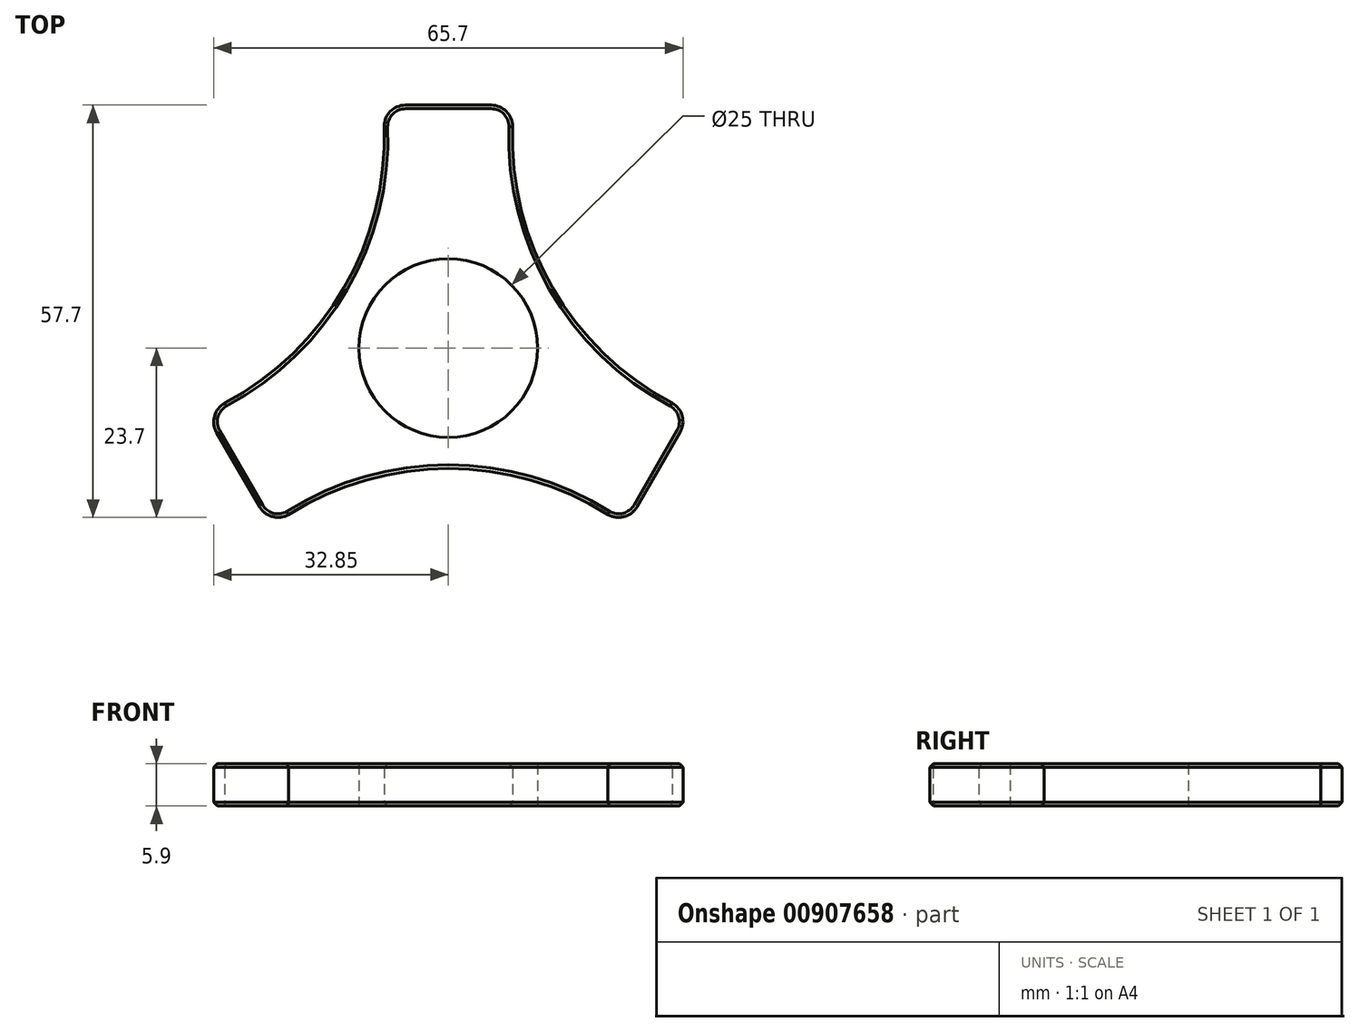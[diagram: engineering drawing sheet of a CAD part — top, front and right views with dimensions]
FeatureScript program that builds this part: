
annotation { "Feature Type Name" : "Feature", "Feature Type Description" : "" }
export const myFeature = defineFeature(function(context is Context, id is Id, definition is map)
    precondition{}
    {
        {
            var Q0;
            Q0=qCreatedBy(makeId("Top.planeOp"),FACE);
            var sketch = newSketch(context, id + "F0", { "sketchPlane" : qUnion([Q0])});
            skPoint(sketch, "E0.center", {"position": v(0, 0) * mm});
            skLineSegment(sketch, "E1", {"start": v(0, 35) * mm, "end": v(0, 0) * mm, "construction": true});
            skArc(sketch, "E2.0", {"start": v(-6, 34) * mm, "mid": v(-8.12, 33.12) * mm, "end": v(-9, 31) * mm});
            skLineSegment(sketch, "E3.0", {"start": v(-6, 34) * mm, "end": v(6, 34) * mm});
            skArc(sketch, "E4.MirrorCS", {"start": v(6, 34) * mm, "mid": v(8.12, 33.12) * mm, "end": v(9, 31) * mm});
            skArc(sketch, "E5.1.0", {"start": v(-26.44, -22.2) * mm, "mid": v(-24.62, -23.6) * mm, "end": v(-22.35, -23.3) * mm});
            skLineSegment(sketch, "E5.1.1", {"start": v(-26.44, -22.2) * mm, "end": v(-32.44, -11.8) * mm});
            skArc(sketch, "E5.1.2", {"start": v(-32.44, -11.8) * mm, "mid": v(-32.74, -9.53) * mm, "end": v(-31.35, -7.7) * mm});
            skArc(sketch, "E5.2.0", {"start": v(32.44, -11.8) * mm, "mid": v(32.74, -9.53) * mm, "end": v(31.35, -7.7) * mm});
            skLineSegment(sketch, "E5.2.1", {"start": v(32.44, -11.8) * mm, "end": v(26.44, -22.2) * mm});
            skArc(sketch, "E5.2.2", {"start": v(26.44, -22.2) * mm, "mid": v(24.62, -23.6) * mm, "end": v(22.35, -23.3) * mm});
            skArc(sketch, "E6", {"start": v(-31.35, -7.7) * mm, "mid": v(-14.6, 8.43) * mm, "end": v(-9, 31) * mm});
            skArc(sketch, "E7.MirrorCS", {"start": v(31.35, -7.7) * mm, "mid": v(14.6, 8.43) * mm, "end": v(9, 31) * mm});
            skArc(sketch, "E8", {"start": v(22.35, -23.3) * mm, "mid": v(0, -16.86) * mm, "end": v(-22.35, -23.3) * mm});
            skCircle(sketch, "E9", {"center": v(0, 0) * mm, "radius": 12.5 * mm});
            skSolve(sketch);
        }
        {
            var Q0;
            Q0 = qSketchRegion(id + "F0", true);
            extrude(context, id + "F1", {"entities" : qUnion([Q0]), "depth" : 5.9 * mm, "offsetDistance" : 25 * mm});
        }
        {
            var Q0;
            Q0=makeQuery(id+"F1.opExtrude","CAP_EDGE",EDGE,{"disambiguationData":[OSD([sQuery(id+"F0.wireOp",EDGE,"E6")])],"isStart":false});
            var Q1;
            Q1=makeQuery(id+"F1.opExtrude","CAP_EDGE",EDGE,{"disambiguationData":[OSD([sQuery(id+"F0.wireOp",EDGE,"E2.0")])],"isStart":false});
            var Q2;
            Q2=makeQuery(id+"F1.opExtrude","CAP_EDGE",EDGE,{"disambiguationData":[OSD([sQuery(id+"F0.wireOp",EDGE,"E3.0")])],"isStart":false});
            var Q3;
            Q3=makeQuery(id+"F1.opExtrude","CAP_EDGE",EDGE,{"disambiguationData":[OSD([sQuery(id+"F0.wireOp",EDGE,"E4.MirrorCS")])],"isStart":false});
            var Q4;
            Q4=makeQuery(id+"F1.opExtrude","CAP_EDGE",EDGE,{"disambiguationData":[OSD([sQuery(id+"F0.wireOp",EDGE,"E7.MirrorCS")])],"isStart":false});
            var Q5;
            Q5=makeQuery(id+"F1.opExtrude","CAP_EDGE",EDGE,{"disambiguationData":[OSD([sQuery(id+"F0.wireOp",EDGE,"E5.2.0")])],"isStart":false});
            var Q6;
            Q6=makeQuery(id+"F1.opExtrude","CAP_EDGE",EDGE,{"disambiguationData":[OSD([sQuery(id+"F0.wireOp",EDGE,"E5.2.1")])],"isStart":false});
            var Q7;
            Q7=makeQuery(id+"F1.opExtrude","CAP_EDGE",EDGE,{"disambiguationData":[OSD([sQuery(id+"F0.wireOp",EDGE,"E5.2.2")])],"isStart":false});
            var Q8;
            Q8=makeQuery(id+"F1.opExtrude","CAP_EDGE",EDGE,{"disambiguationData":[OSD([sQuery(id+"F0.wireOp",EDGE,"E8")])],"isStart":false});
            var Q9;
            Q9=makeQuery(id+"F1.opExtrude","CAP_EDGE",EDGE,{"disambiguationData":[OSD([sQuery(id+"F0.wireOp",EDGE,"E5.1.0")])],"isStart":false});
            var Q10;
            Q10=makeQuery(id+"F1.opExtrude","CAP_EDGE",EDGE,{"disambiguationData":[OSD([sQuery(id+"F0.wireOp",EDGE,"E5.1.1")])],"isStart":false});
            var Q11;
            Q11=makeQuery(id+"F1.opExtrude","CAP_EDGE",EDGE,{"disambiguationData":[OSD([sQuery(id+"F0.wireOp",EDGE,"E5.1.2")])],"isStart":false});
            chamfer(context, id + "F2", {"entities" : qUnion([Q0, Q1, Q2, Q3, Q4, Q5, Q6, Q7, Q8, Q9, Q10, Q11]), "width" : .5 * mm, "tangentPropagation" : true});
        }
        {
            var Q0;
            Q0=makeQuery(id+"F1.opExtrude","CAP_EDGE",EDGE,{"disambiguationData":[OSD([sQuery(id+"F0.wireOp",EDGE,"E6")])],"isStart":true});
            var Q1;
            Q1=makeQuery(id+"F1.opExtrude","CAP_EDGE",EDGE,{"disambiguationData":[OSD([sQuery(id+"F0.wireOp",EDGE,"E5.1.1")])],"isStart":true});
            var Q2;
            Q2=makeQuery(id+"F1.opExtrude","CAP_EDGE",EDGE,{"disambiguationData":[OSD([sQuery(id+"F0.wireOp",EDGE,"E5.1.0")])],"isStart":true});
            var Q3;
            Q3=makeQuery(id+"F1.opExtrude","CAP_EDGE",EDGE,{"disambiguationData":[OSD([sQuery(id+"F0.wireOp",EDGE,"E8")])],"isStart":true});
            var Q4;
            Q4=makeQuery(id+"F1.opExtrude","CAP_EDGE",EDGE,{"disambiguationData":[OSD([sQuery(id+"F0.wireOp",EDGE,"E5.1.2")])],"isStart":true});
            var Q5;
            Q5=makeQuery(id+"F1.opExtrude","CAP_EDGE",EDGE,{"disambiguationData":[OSD([sQuery(id+"F0.wireOp",EDGE,"E5.2.2")])],"isStart":true});
            var Q6;
            Q6=makeQuery(id+"F1.opExtrude","CAP_EDGE",EDGE,{"disambiguationData":[OSD([sQuery(id+"F0.wireOp",EDGE,"E5.2.1")])],"isStart":true});
            var Q7;
            Q7=makeQuery(id+"F1.opExtrude","CAP_EDGE",EDGE,{"disambiguationData":[OSD([sQuery(id+"F0.wireOp",EDGE,"E7.MirrorCS")])],"isStart":true});
            var Q8;
            Q8=makeQuery(id+"F1.opExtrude","CAP_EDGE",EDGE,{"disambiguationData":[OSD([sQuery(id+"F0.wireOp",EDGE,"E4.MirrorCS")])],"isStart":true});
            var Q9;
            Q9=makeQuery(id+"F1.opExtrude","CAP_EDGE",EDGE,{"disambiguationData":[OSD([sQuery(id+"F0.wireOp",EDGE,"E3.0")])],"isStart":true});
            var Q10;
            Q10=makeQuery(id+"F1.opExtrude","CAP_EDGE",EDGE,{"disambiguationData":[OSD([sQuery(id+"F0.wireOp",EDGE,"E2.0")])],"isStart":true});
            chamfer(context, id + "F3", {"entities" : qUnion([Q0, Q1, Q2, Q3, Q4, Q5, Q6, Q7, Q8, Q9, Q10]), "width" : .5 * mm, "tangentPropagation" : true});
        }
    });
